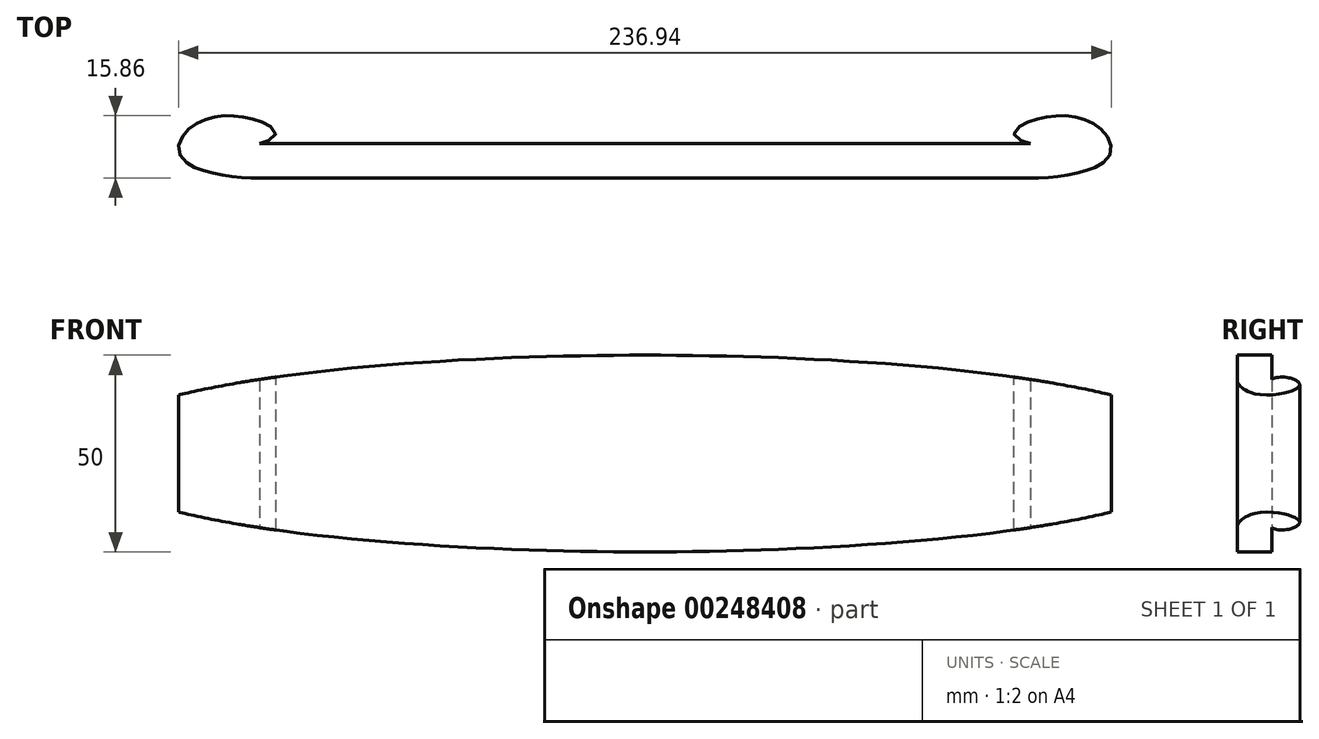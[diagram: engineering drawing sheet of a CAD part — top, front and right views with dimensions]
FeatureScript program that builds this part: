
annotation { "Feature Type Name" : "Feature", "Feature Type Description" : "" }
export const myFeature = defineFeature(function(context is Context, id is Id, definition is map)
    precondition{}
    {
        {
            var Q0;
            Q0=qCreatedBy(makeId("Top.planeOp"),FACE);
            var sketch = newSketch(context, id + "F0", { "sketchPlane" : qUnion([Q0])});
            skLineSegment(sketch, "E0", {"start": v(0, 0) * mm, "end": v(100, 0) * mm});
            skLineSegment(sketch, "E1", {"start": v(0, 0) * mm, "end": v(0, 8.77) * mm});
            skLineSegment(sketch, "E2", {"start": v(0, 8.77) * mm, "end": v(97.93, 8.77) * mm});
            skLineSegment(sketch, "E3", {"start": v(0, 5.33) * mm, "end": v(150, 5.33) * mm, "construction": true});
            skFitSpline(sketch, "E4", {"points": [v(100, 0) * mm, v(117.84, 5.33) * mm, v(105.7, 15.86) * mm, v(97.93, 8.77) * mm], "startDerivative": vector(26.58, 0) * mm, "endDerivative": vector(107.1, -25.92) * mm});
            skSolve(sketch);
        }
        {
            var Q0;
            Q0 = qSketchRegion(id + "F0", true);
            extrude(context, id + "F1", {"entities" : qUnion([Q0]), "depth" : 25 * mm, "hasSecondDirection" : true, "secondDirectionOppositeDirection" : true, "secondDirectionDepth" : 25 * mm});
        }
        {
            var Q0;
            Q0=qCreatedBy(makeId("Front.planeOp"),FACE);
            var sketch = newSketch(context, id + "F2", { "sketchPlane" : qUnion([Q0])});
            skLineSegment(sketch, "E5", {"start": v(0, 0) * mm, "end": v(147.1, 0) * mm, "construction": true});
            skFitSpline(sketch, "E6", {"points": [v(0, 25) * mm, v(147.1, 0) * mm], "startDerivative": vector(160.61, 0) * mm, "endDerivative": vector(28.28, -59.44) * mm});
            skFitSpline(sketch, "E7.MirrorCS", {"points": [v(0, -25) * mm, v(147.1, 0) * mm], "startDerivative": vector(160.61, 0) * mm, "endDerivative": vector(28.28, 59.44) * mm});
            skLineSegment(sketch, "E8", {"start": v(147.1, 0) * mm, "end": v(149.68, 31) * mm});
            skLineSegment(sketch, "E9", {"start": v(0, 25) * mm, "end": v(149.68, 31) * mm});
            skLineSegment(sketch, "E10.MirrorCS", {"start": v(147.1, 0) * mm, "end": v(149.68, -31) * mm});
            skLineSegment(sketch, "E11", {"start": v(149.68, -31) * mm, "end": v(0, -25) * mm});
            skSolve(sketch);
        }
        {
            var Q0;
            Q0 = qSketchRegion(id + "F2", true);
            extrude(context, id + "F3", {"entities" : qUnion([Q0]), "operationType" : NewBodyOperationType.REMOVE, "endBound" : BoundingType.THROUGH_ALL, "oppositeDirection" : true, "depth" : 25 * mm});
        }
        {
            var Q0;
            Q0=makeQuery(id+"F1.opExtrude","SWEPT_BODY",BODY,{"disambiguationData":[OSD([sQuery(id+"F0.wireOp",EDGE,"E0"),sQuery(id+"F0.wireOp",EDGE,"E1"),sQuery(id+"F0.wireOp",EDGE,"E2"),sQuery(id+"F0.wireOp",EDGE,"E4")])]});
            var Q1;
            Q1=qCreatedBy(makeId("Right.planeOp"),FACE);
            mirror(context, id + "F4", {"operationType" : NewBodyOperationType.ADD, "entities" : qUnion([Q0]), "mirrorPlane" : qUnion([Q1])});
        }
    });
